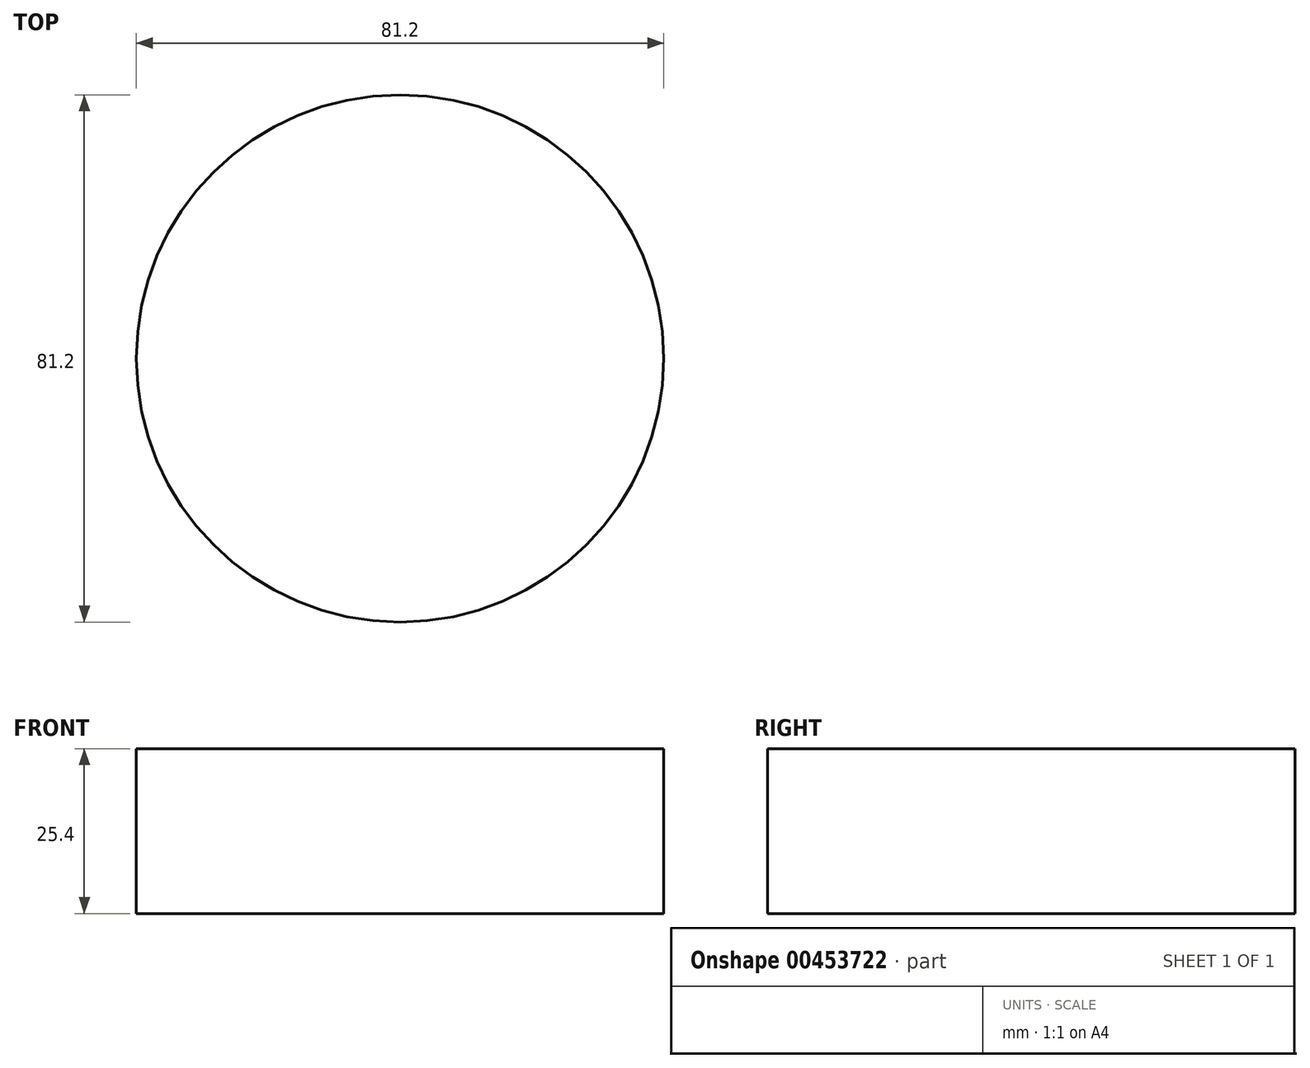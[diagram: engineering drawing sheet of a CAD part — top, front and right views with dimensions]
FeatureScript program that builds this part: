
annotation { "Feature Type Name" : "Feature", "Feature Type Description" : "" }
export const myFeature = defineFeature(function(context is Context, id is Id, definition is map)
    precondition{}
    {
        {
            var Q0;
            Q0=qCreatedBy(makeId("Top.planeOp"),FACE);
            var sketch = newSketch(context, id + "F0", { "sketchPlane" : qUnion([Q0])});
            skCircle(sketch, "E0", {"center": v(0, 0) * mm, "radius": 40.6 * mm});
            skSolve(sketch);
        }
        {
            var Q0;
            Q0 = qSketchRegion(id + "F0", true);
            extrude(context, id + "F1", {"entities" : qUnion([Q0]), "depth" : 25.4 * mm});
        }
    });
